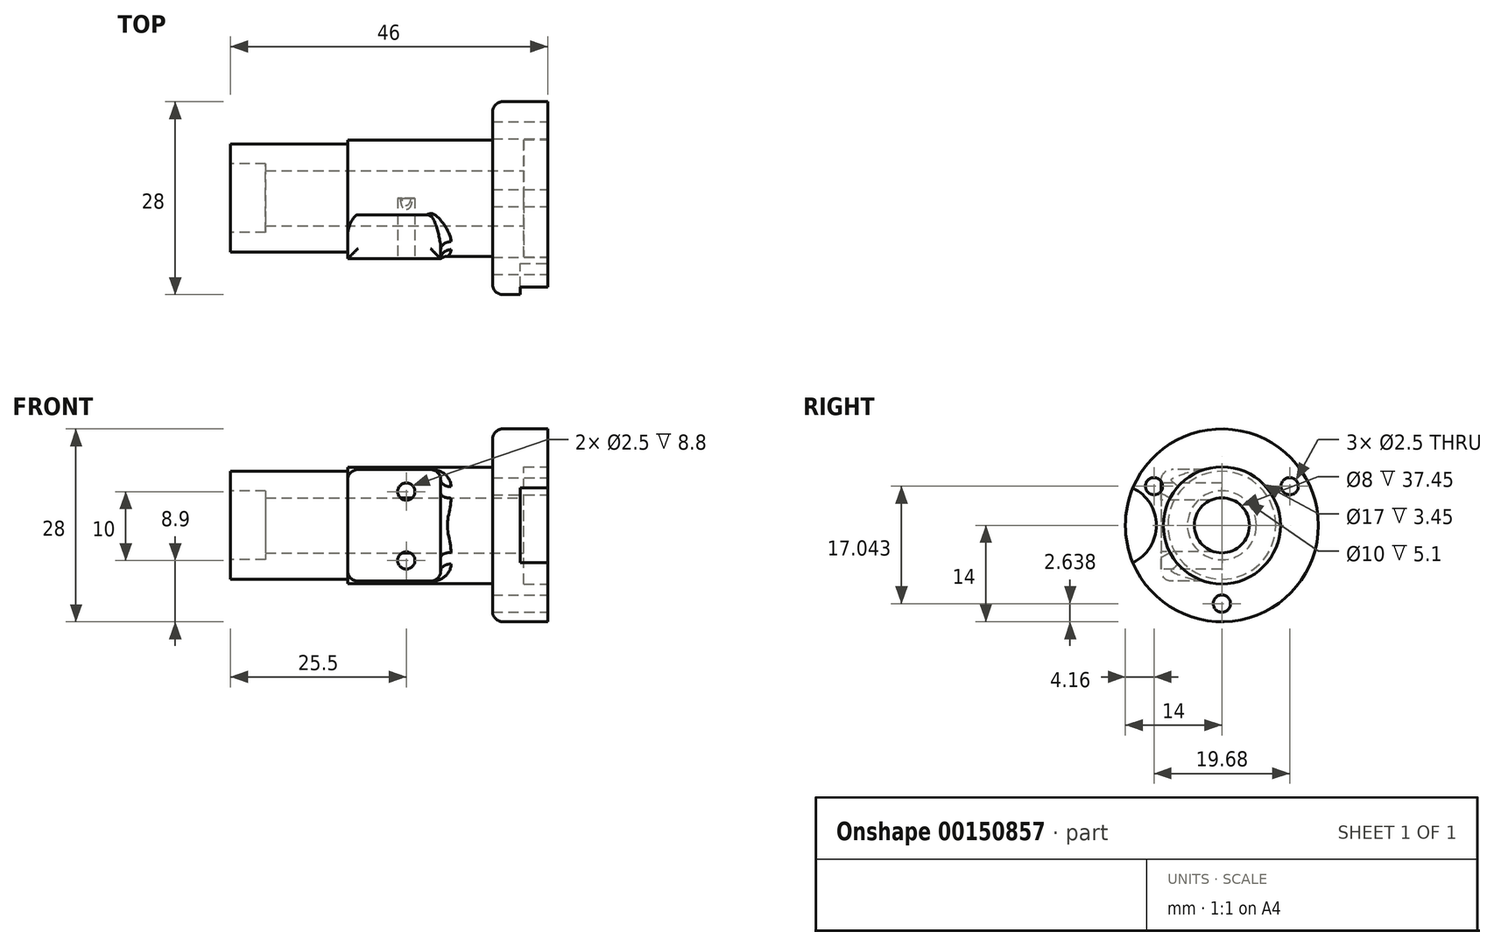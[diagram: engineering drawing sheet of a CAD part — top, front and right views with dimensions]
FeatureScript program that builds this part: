
annotation { "Feature Type Name" : "Feature", "Feature Type Description" : "" }
export const myFeature = defineFeature(function(context is Context, id is Id, definition is map)
    precondition{}
    {
        {
            var Q0;
            Q0=qCreatedBy(makeId("Right.planeOp"),FACE);
            var sketch = newSketch(context, id + "F0", { "sketchPlane" : qUnion([Q0])});
            skCircle(sketch, "E0", {"center": v(0, 0) * mm, "radius": 14 * mm});
            skSolve(sketch);
        }
        {
            var Q0;
            Q0=makeQuery(id+"F0.imprint","IMPRINT",FACE,{"disambiguationData":[TD([[makeQuery(id+"F0.imprint","IMPRINT",EDGE,{"derivedFrom":sQuery(id+"F0.wireOp",EDGE,"E0")}),1.0]])]});
            extrude(context, id + "F1", {"entities" : qUnion([Q0]), "depth" : 8 * mm});
        }
        {
            var Q0;
            Q0=makeQuery(id+"F1.opExtrude","CAP_FACE",FACE,{"disambiguationData":[OSD([sQuery(id+"F0.wireOp",EDGE,"E0")])],"isStart":false});
            var sketch = newSketch(context, id + "F2", { "sketchPlane" : qUnion([Q0])});
            skCircle(sketch, "E1", {"center": v(0, 0) * mm, "radius": 8.5 * mm});
            skSolve(sketch);
        }
        {
            var Q0;
            Q0=qSketchRegion(id+"F2",true);
            extrude(context, id + "F3", {"entities" : qUnion([Q0]), "operationType" : NewBodyOperationType.REMOVE, "oppositeDirection" : true, "depth" : 3.45 * mm});
        }
        {
            var Q0;
            Q0=makeQuery(id+"F1.opExtrude","CAP_FACE",FACE,{"disambiguationData":[OSD([sQuery(id+"F0.wireOp",EDGE,"E0")])],"isStart":false});
            var sketch = newSketch(context, id + "F4", { "sketchPlane" : qUnion([Q0])});
            skCircle(sketch, "E2", {"center": v(0, 0) * mm, "radius": 11.36 * mm, "construction": true});
            skCircle(sketch, "E3", {"center": v(0, -11.36) * mm, "radius": 1.25 * mm});
            skCircle(sketch, "E4.1.0", {"center": v(9.84, 5.68) * mm, "radius": 1.25 * mm});
            skCircle(sketch, "E4.2.0", {"center": v(-9.84, 5.68) * mm, "radius": 1.25 * mm});
            skSolve(sketch);
        }
        {
            var Q0;
            Q0=makeQuery(id+"F4.imprint","IMPRINT",FACE,{"disambiguationData":[TD([[makeQuery(id+"F4.imprint","IMPRINT",EDGE,{"derivedFrom":sQuery(id+"F4.wireOp",EDGE,"E4.2.0")}),1.0]])]});
            var Q1;
            Q1=makeQuery(id+"F4.imprint","IMPRINT",FACE,{"disambiguationData":[TD([[makeQuery(id+"F4.imprint","IMPRINT",EDGE,{"derivedFrom":sQuery(id+"F4.wireOp",EDGE,"E4.1.0")}),1.0]])]});
            var Q2;
            Q2=makeQuery(id+"F4.imprint","IMPRINT",FACE,{"disambiguationData":[TD([[makeQuery(id+"F4.imprint","IMPRINT",EDGE,{"derivedFrom":sQuery(id+"F4.wireOp",EDGE,"E3")}),1.0]])]});
            extrude(context, id + "F5", {"entities" : qUnion([Q0, Q1, Q2]), "operationType" : NewBodyOperationType.REMOVE, "endBound" : BoundingType.THROUGH_ALL, "oppositeDirection" : true, "depth" : 25 * mm});
        }
        {
            var Q0;
            Q0=makeQuery(id+"F1.opExtrude","CAP_FACE",FACE,{"disambiguationData":[OSD([sQuery(id+"F0.wireOp",EDGE,"E0")])],"isStart":true});
            var sketch = newSketch(context, id + "F6", { "sketchPlane" : qUnion([Q0])});
            skCircle(sketch, "E5", {"center": v(0, 0) * mm, "radius": 8.45 * mm});
            skSolve(sketch);
        }
        {
            var Q0;
            Q0=makeQuery(id+"F6.imprint","IMPRINT",FACE,{"disambiguationData":[TD([[makeQuery(id+"F6.imprint","IMPRINT",EDGE,{"derivedFrom":sQuery(id+"F6.wireOp",EDGE,"E5")}),1.0]])]});
            extrude(context, id + "F7", {"entities" : qUnion([Q0]), "operationType" : NewBodyOperationType.ADD, "depth" : 21 * mm});
        }
        {
            var Q0;
            Q0=makeQuery(id+"F7.opExtrude","CAP_FACE",FACE,{"disambiguationData":[OSD([sQuery(id+"F6.wireOp",EDGE,"E5")])],"isStart":false});
            var sketch = newSketch(context, id + "F8", { "sketchPlane" : qUnion([Q0])});
            skCircle(sketch, "E6", {"center": v(0, 0) * mm, "radius": 7.82 * mm});
            skSolve(sketch);
        }
        {
            var Q0;
            Q0 = qSketchRegion(id + "F8", true);
            extrude(context, id + "F9", {"entities" : qUnion([Q0]), "operationType" : NewBodyOperationType.ADD, "depth" : 17 * mm});
        }
        {
            var Q0;
            Q0=qCreatedBy(makeId("Top.planeOp"),FACE);
            var sketch = newSketch(context, id + "F10", { "sketchPlane" : qUnion([Q0])});
            skLineSegment(sketch, "E7.bottom", {"start": v(-21, 0) * mm, "end": v(-7.5, 0) * mm});
            skLineSegment(sketch, "E7.top", {"start": v(-21, -8.8) * mm, "end": v(-7.5, -8.8) * mm});
            skLineSegment(sketch, "E7.left", {"start": v(-21, 0) * mm, "end": v(-21, -8.8) * mm});
            skLineSegment(sketch, "E7.right", {"start": v(-7.5, 0) * mm, "end": v(-7.5, -8.8) * mm});
            skSolve(sketch);
        }
        {
            var Q0;
            Q0=makeQuery(id+"F10.imprint","IMPRINT",FACE,{"disambiguationData":[TD([[makeQuery(id+"F10.imprint","IMPRINT",EDGE,{"derivedFrom":sQuery(id+"F10.wireOp",EDGE,"E7.bottom")}),-1.0]])]});
            extrude(context, id + "F11", {"entities" : qUnion([Q0]), "operationType" : NewBodyOperationType.ADD, "endBound" : BoundingType.SYMMETRIC, "depth" : 16.2 * mm});
        }
        {
            var Q0;
            Q0=makeQuery(id+"F1.opExtrude","CAP_FACE",FACE,{"disambiguationData":[OSD([sQuery(id+"F0.wireOp",EDGE,"E0")])],"isStart":false});
            var sketch = newSketch(context, id + "F12", { "sketchPlane" : qUnion([Q0])});
            skCircle(sketch, "E8", {"center": v(0, 0) * mm, "radius": 4 * mm});
            skSolve(sketch);
        }
        {
            var Q0;
            Q0=makeQuery(id+"F12.imprint","IMPRINT",FACE,{"disambiguationData":[TD([[makeQuery(id+"F12.imprint","IMPRINT",EDGE,{"derivedFrom":sQuery(id+"F12.wireOp",EDGE,"E8")}),1.0]])]});
            extrude(context, id + "F13", {"entities" : qUnion([Q0]), "operationType" : NewBodyOperationType.REMOVE, "endBound" : BoundingType.THROUGH_ALL, "oppositeDirection" : true, "depth" : 25 * mm});
        }
        {
            var Q0;
            Q0=makeQuery(id+"F9.opExtrude","CAP_FACE",FACE,{"disambiguationData":[OSD([sQuery(id+"F8.wireOp",EDGE,"E6")])],"isStart":false});
            var sketch = newSketch(context, id + "F14", { "sketchPlane" : qUnion([Q0])});
            skCircle(sketch, "E9", {"center": v(0, 0) * mm, "radius": 5 * mm});
            skSolve(sketch);
        }
        {
            var Q0;
            Q0=makeQuery(id+"F14.imprint","IMPRINT",FACE,{"disambiguationData":[TD([[makeQuery(id+"F14.imprint","IMPRINT",EDGE,{"derivedFrom":sQuery(id+"F14.wireOp",EDGE,"E9")}),1.0]])]});
            extrude(context, id + "F15", {"entities" : qUnion([Q0]), "operationType" : NewBodyOperationType.REMOVE, "oppositeDirection" : true, "depth" : 5.1 * mm});
        }
        {
            var Q0;
            Q0=makeQuery(id+"F11.opExtrude","SWEPT_FACE",FACE,{"disambiguationData":[OSD([sQuery(id+"F10.wireOp",EDGE,"E7.top")])]});
            var sketch = newSketch(context, id + "F16", { "sketchPlane" : qUnion([Q0])});
            skCircle(sketch, "E10", {"center": v(-12.5, -5.1) * mm, "radius": 1.25 * mm});
            skLineSegment(sketch, "E11", {"start": v(-12.5, -16.17) * mm, "end": v(-12.5, 16.97) * mm, "construction": true});
            skCircle(sketch, "E12", {"center": v(-12.5, 4.9) * mm, "radius": 1.25 * mm});
            skSolve(sketch);
        }
        {
            var Q0;
            Q0=makeQuery(id+"F16.imprint","IMPRINT",FACE,{"disambiguationData":[TD([[makeQuery(id+"F16.imprint","IMPRINT",EDGE,{"derivedFrom":sQuery(id+"F16.wireOp",EDGE,"E12")}),1.0]])]});
            var Q1;
            Q1=makeQuery(id+"F16.imprint","IMPRINT",FACE,{"disambiguationData":[TD([[makeQuery(id+"F16.imprint","IMPRINT",EDGE,{"derivedFrom":sQuery(id+"F16.wireOp",EDGE,"E10")}),1.0]])]});
            extrude(context, id + "F17", {"entities" : qUnion([Q0, Q1]), "operationType" : NewBodyOperationType.REMOVE, "oppositeDirection" : true, "depth" : 8.8 * mm});
        }
        {
            var Q0;
            Q0=makeQuery(id+"F1.opExtrude","CAP_FACE",FACE,{"disambiguationData":[OSD([sQuery(id+"F0.wireOp",EDGE,"E0")])],"isStart":false});
            var sketch = newSketch(context, id + "F18", { "sketchPlane" : qUnion([Q0])});
            skCircle(sketch, "E13", {"center": v(-15.5, 0) * mm, "radius": 6 * mm});
            skSolve(sketch);
        }
        {
            var Q0;
            Q0=qSketchRegion(id+"F18",true);
            extrude(context, id + "F19", {"entities" : qUnion([Q0]), "operationType" : NewBodyOperationType.REMOVE, "oppositeDirection" : true, "depth" : 4 * mm});
        }
        {
            var Q0;
            Q0=makeQuery(id+"F11.opExtrude","CAP_EDGE",EDGE,{"disambiguationData":[OSD([sQuery(id+"F10.wireOp",EDGE,"E7.right")])],"isStart":false});
            var Q1;
            Q1=makeQuery(id+"F11.opExtrude","CAP_EDGE",EDGE,{"disambiguationData":[OSD([sQuery(id+"F10.wireOp",EDGE,"E7.right")])],"isStart":true});
            var Q2;
            Q2=makeQuery(id+"F11.opExtrude","CAP_EDGE",EDGE,{"disambiguationData":[OSD([sQuery(id+"F10.wireOp",EDGE,"E7.top")])],"isStart":false});
            var Q3;
            Q3=makeQuery(id+"F11.opExtrude","CAP_EDGE",EDGE,{"disambiguationData":[OSD([sQuery(id+"F10.wireOp",EDGE,"E7.left")])],"isStart":true});
            var Q4;
            Q4=makeQuery(id+"F11.opExtrude","CAP_EDGE",EDGE,{"disambiguationData":[OSD([sQuery(id+"F10.wireOp",EDGE,"E7.left")])],"isStart":false});
            var Q5;
            Q5=makeQuery(id+"F11.opExtrude","CAP_EDGE",EDGE,{"disambiguationData":[OSD([sQuery(id+"F10.wireOp",EDGE,"E7.top")])],"isStart":true});
            var Q6;
            Q6=makeQuery(id+"F11.boolean.opBoolean","INTERSECT",EDGE,{"derivedFrom":[makeQuery(id+"F7.opExtrude","SWEPT_FACE",FACE,{"disambiguationData":[OSD([sQuery(id+"F6.wireOp",EDGE,"E5")])]}),makeQuery(id+"F11.opExtrude","SWEPT_FACE",FACE,{"disambiguationData":[OSD([sQuery(id+"F10.wireOp",EDGE,"E7.right")])]})]});
            fillet(context, id + "F20", {"entities" : qUnion([Q0, Q1, Q2, Q3, Q4, Q5, Q6]), "radius" : 1.5 * mm, "allowEdgeOverflow" : false});
        }
        {
            var Q0;
            Q0=makeQuery(id+"F7.opExtrude","CAP_EDGE",EDGE,{"disambiguationData":[OSD([sQuery(id+"F6.wireOp",EDGE,"E5")])],"isStart":true});
            var Q1;
            Q1=makeQuery(id+"F1.opExtrude","CAP_EDGE",EDGE,{"disambiguationData":[OSD([sQuery(id+"F0.wireOp",EDGE,"E0")])],"isStart":true});
            fillet(context, id + "F21", {"entities" : qUnion([Q0, Q1]), "radius" : 1.5 * mm, "tangentPropagation" : true, "allowEdgeOverflow" : false});
        }
    });
